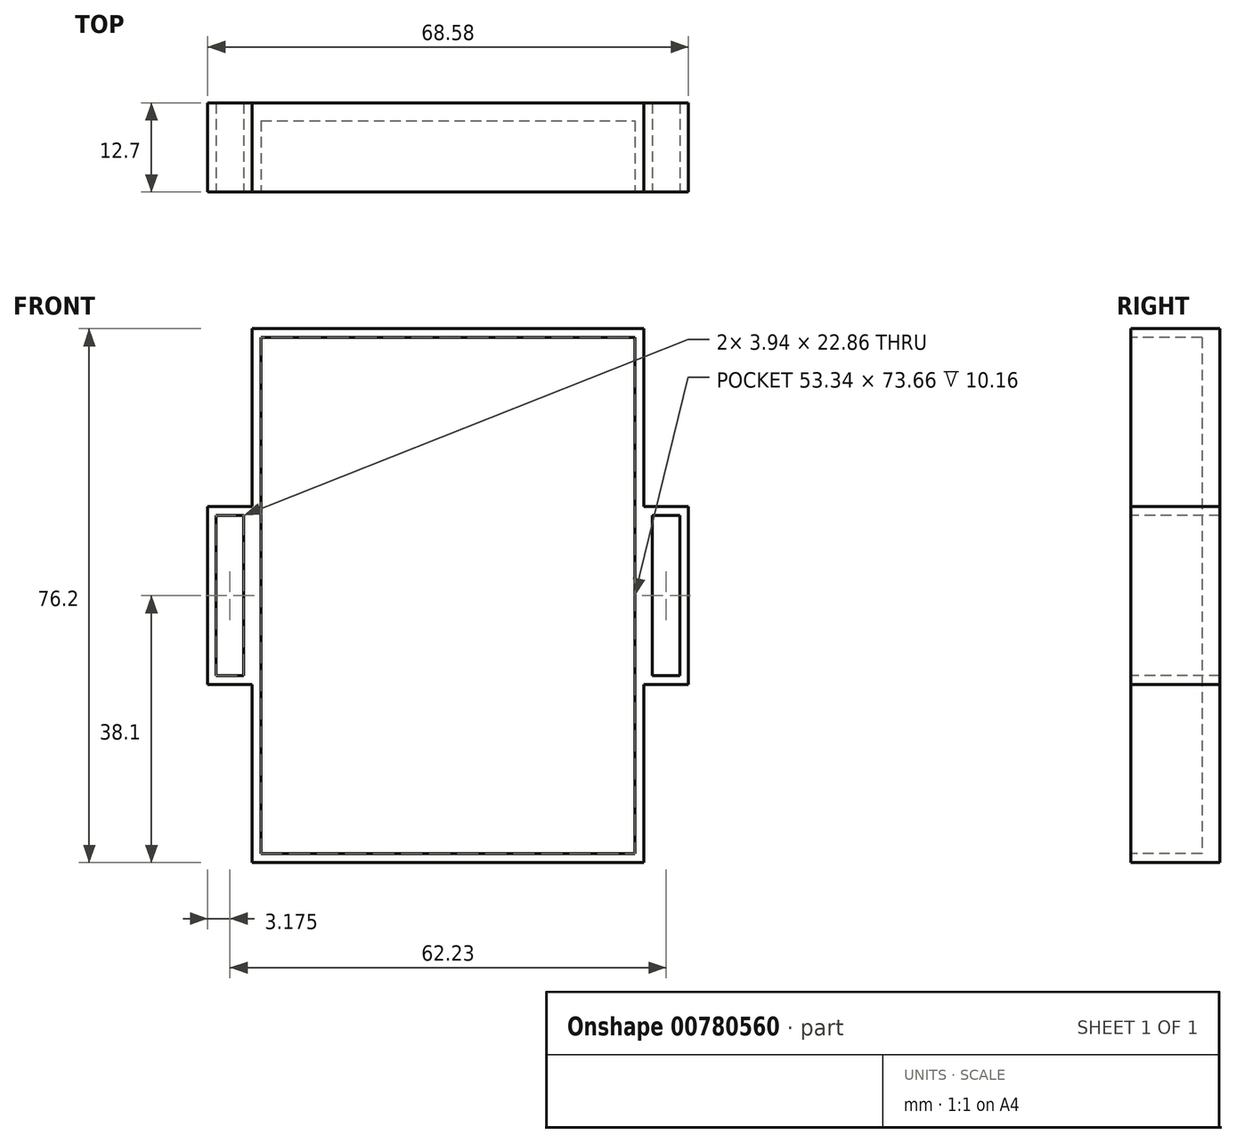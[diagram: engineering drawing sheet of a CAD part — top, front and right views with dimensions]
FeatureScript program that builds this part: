
annotation { "Feature Type Name" : "Feature", "Feature Type Description" : "" }
export const myFeature = defineFeature(function(context is Context, id is Id, definition is map)
    precondition{}
    {
        {
            var Q0;
            Q0=qCreatedBy(makeId("Front.planeOp"),FACE);
            var sketch = newSketch(context, id + "F0", { "sketchPlane" : qUnion([Q0])});
            skLineSegment(sketch, "E0.bottom", {"start": v(-27.94, 38.1) * mm, "end": v(27.94, 38.1) * mm});
            skLineSegment(sketch, "E0.top", {"start": v(-27.94, -38.1) * mm, "end": v(27.94, -38.1) * mm});
            skLineSegment(sketch, "E0.left", {"start": v(-27.94, 38.1) * mm, "end": v(-27.94, -38.1) * mm});
            skLineSegment(sketch, "E0.right", {"start": v(27.94, 38.1) * mm, "end": v(27.94, -38.1) * mm});
            skPoint(sketch, "E0.middle", {"position": v(0, 0) * mm});
            skSolve(sketch);
        }
        {
            var Q0;
            Q0=makeQuery(id+"F0.imprint","IMPRINT",FACE,{"disambiguationData":[TD([[makeQuery(id+"F0.imprint","IMPRINT",EDGE,{"derivedFrom":sQuery(id+"F0.wireOp",EDGE,"E0.bottom")}),-1.0]])]});
            extrude(context, id + "F1", {"entities" : qUnion([Q0]), "depth" : 12.7 * mm, "offsetDistance" : 25.4 * mm});
        }
        {
            var Q0;
            Q0=makeQuery(id+"F1.opExtrude","CAP_FACE",FACE,{"disambiguationData":[OSD([sQuery(id+"F0.wireOp",EDGE,"E0.bottom"),sQuery(id+"F0.wireOp",EDGE,"E0.top"),sQuery(id+"F0.wireOp",EDGE,"E0.left"),sQuery(id+"F0.wireOp",EDGE,"E0.right")])],"isStart":false});
            var sketch = newSketch(context, id + "F2", { "sketchPlane" : qUnion([Q0])});
            skLineSegment(sketch, "E1.bottom", {"start": v(-26.67, 36.83) * mm, "end": v(26.67, 36.83) * mm});
            skLineSegment(sketch, "E1.top", {"start": v(-26.67, -36.83) * mm, "end": v(26.67, -36.83) * mm});
            skLineSegment(sketch, "E1.left", {"start": v(-26.67, 36.83) * mm, "end": v(-26.67, -36.83) * mm});
            skLineSegment(sketch, "E1.right", {"start": v(26.67, 36.83) * mm, "end": v(26.67, -36.83) * mm});
            skPoint(sketch, "E1.middle", {"position": v(0, 0) * mm});
            skSolve(sketch);
        }
        {
            var Q0;
            Q0 = qSketchRegion(id + "F2", true);
            extrude(context, id + "F3", {"entities" : qUnion([Q0]), "operationType" : NewBodyOperationType.REMOVE, "oppositeDirection" : true, "depth" : 10.16 * mm, "offsetDistance" : 25.4 * mm});
        }
        {
            var Q0;
            Q0=makeQuery(id+"F1.opExtrude","SWEPT_FACE",FACE,{"disambiguationData":[OSD([sQuery(id+"F0.wireOp",EDGE,"E0.right")])]});
            var sketch = newSketch(context, id + "F4", { "sketchPlane" : qUnion([Q0])});
            skLineSegment(sketch, "E2.bottom", {"start": v(0, -12.7) * mm, "end": v(-12.7, -12.7) * mm});
            skLineSegment(sketch, "E2.top", {"start": v(0, 12.7) * mm, "end": v(-12.7, 12.7) * mm});
            skLineSegment(sketch, "E2.left", {"start": v(0, -12.7) * mm, "end": v(0, 12.7) * mm});
            skLineSegment(sketch, "E2.right", {"start": v(-12.7, -12.7) * mm, "end": v(-12.7, 12.7) * mm});
            skPoint(sketch, "E2.middle", {"position": v(-6.35, 0) * mm});
            skPoint(sketch, "E2.middle.positionSnap0", {"position": v(-6.35, 38.1) * mm});
            skPoint(sketch, "E2.centerSnap0", {"position": v(-6.35, 38.1) * mm});
            skSolve(sketch);
        }
        {
            var Q0;
            Q0 = qSketchRegion(id + "F4", true);
            extrude(context, id + "F5", {"entities" : qUnion([Q0]), "operationType" : NewBodyOperationType.ADD, "depth" : 6.35 * mm, "offsetDistance" : 25.4 * mm});
        }
        {
            var Q0;
            Q0=makeQuery(id+"F1.opExtrude","SWEPT_FACE",FACE,{"disambiguationData":[OSD([sQuery(id+"F0.wireOp",EDGE,"E0.left")])]});
            var sketch = newSketch(context, id + "F6", { "sketchPlane" : qUnion([Q0])});
            skLineSegment(sketch, "E3.bottom", {"start": v(0, 12.7) * mm, "end": v(12.7, 12.7) * mm});
            skLineSegment(sketch, "E3.top", {"start": v(0, -12.7) * mm, "end": v(12.7, -12.7) * mm});
            skLineSegment(sketch, "E3.left", {"start": v(0, 12.7) * mm, "end": v(0, -12.7) * mm});
            skLineSegment(sketch, "E3.right", {"start": v(12.7, 12.7) * mm, "end": v(12.7, -12.7) * mm});
            skPoint(sketch, "E3.middle", {"position": v(6.35, 0) * mm});
            skPoint(sketch, "E3.middle.positionSnap0", {"position": v(6.35, 38.1) * mm});
            skPoint(sketch, "E3.centerSnap0", {"position": v(6.35, 38.1) * mm});
            skSolve(sketch);
        }
        {
            var Q0;
            Q0 = qSketchRegion(id + "F6", true);
            extrude(context, id + "F7", {"entities" : qUnion([Q0]), "operationType" : NewBodyOperationType.ADD, "depth" : 6.35 * mm, "offsetDistance" : 25.4 * mm});
        }
        {
            var Q0;
            Q0=makeQuery(id+"F7.boolean.opBoolean","MERGE",FACE,{"derivedFrom":[makeQuery(id+"F5.boolean.opBoolean","MERGE",FACE,{"derivedFrom":[makeQuery(id+"F1.opExtrude","CAP_FACE",FACE,{"disambiguationData":[OSD([sQuery(id+"F0.wireOp",EDGE,"E0.bottom"),sQuery(id+"F0.wireOp",EDGE,"E0.top"),sQuery(id+"F0.wireOp",EDGE,"E0.left"),sQuery(id+"F0.wireOp",EDGE,"E0.right")])],"isStart":false}),makeQuery(id+"F5.opExtrude","SWEPT_FACE",FACE,{"disambiguationData":[OSD([sQuery(id+"F4.wireOp",EDGE,"E2.right")])]})]}),makeQuery(id+"F7.opExtrude","SWEPT_FACE",FACE,{"disambiguationData":[OSD([sQuery(id+"F6.wireOp",EDGE,"E3.right")])]})]});
            var sketch = newSketch(context, id + "F8", { "sketchPlane" : qUnion([Q0])});
            skLineSegment(sketch, "E4.bottom", {"start": v(-33.08, 11.43) * mm, "end": v(-29.15, 11.43) * mm});
            skLineSegment(sketch, "E4.top", {"start": v(-33.08, -11.43) * mm, "end": v(-29.15, -11.43) * mm});
            skLineSegment(sketch, "E4.left", {"start": v(-33.08, 11.43) * mm, "end": v(-33.08, -11.43) * mm});
            skLineSegment(sketch, "E4.right", {"start": v(-29.15, 11.43) * mm, "end": v(-29.15, -11.43) * mm});
            skPoint(sketch, "E4.middle", {"position": v(-31.12, 0) * mm});
            skPoint(sketch, "E4.middle.positionSnap0", {"position": v(-31.12, 12.7) * mm});
            skPoint(sketch, "E4.middle.positionSnap1", {"position": v(-34.3, 0) * mm});
            skPoint(sketch, "E4.centerSnap0", {"position": v(-31.12, 12.7) * mm});
            skPoint(sketch, "E4.centerSnap1", {"position": v(-34.3, 0) * mm});
            skLineSegment(sketch, "E5.bottom", {"start": v(29.15, 11.43) * mm, "end": v(33.08, 11.43) * mm});
            skLineSegment(sketch, "E5.top", {"start": v(29.15, -11.43) * mm, "end": v(33.08, -11.43) * mm});
            skLineSegment(sketch, "E5.left", {"start": v(29.15, 11.43) * mm, "end": v(29.15, -11.43) * mm});
            skLineSegment(sketch, "E5.right", {"start": v(33.08, 11.43) * mm, "end": v(33.08, -11.43) * mm});
            skPoint(sketch, "E5.middle", {"position": v(31.12, 0) * mm});
            skPoint(sketch, "E5.middle.positionSnap0", {"position": v(34.3, 0) * mm});
            skPoint(sketch, "E5.middle.positionSnap1", {"position": v(31.12, 12.7) * mm});
            skPoint(sketch, "E5.centerSnap0", {"position": v(34.3, 0) * mm});
            skPoint(sketch, "E5.centerSnap1", {"position": v(31.12, 12.7) * mm});
            skSolve(sketch);
        }
        {
            var Q0;
            Q0 = qSketchRegion(id + "F8", true);
            extrude(context, id + "F9", {"entities" : qUnion([Q0]), "operationType" : NewBodyOperationType.REMOVE, "oppositeDirection" : true, "depth" : 25.4 * mm, "offsetDistance" : 25.4 * mm});
        }
    });
